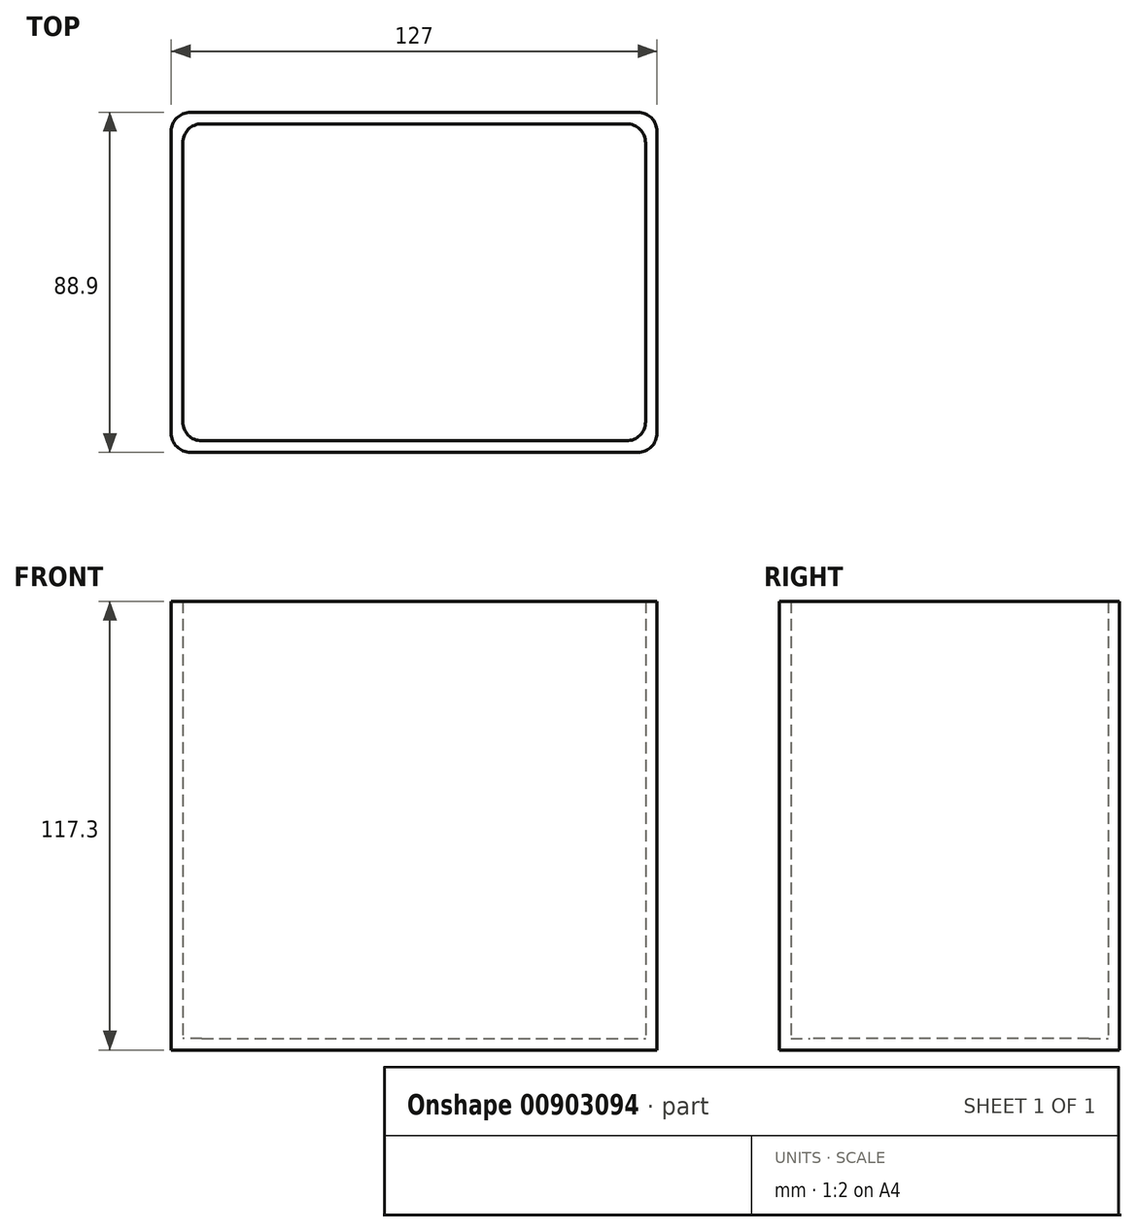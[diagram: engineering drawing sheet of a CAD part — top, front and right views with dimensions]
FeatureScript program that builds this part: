
annotation { "Feature Type Name" : "Feature", "Feature Type Description" : "" }
export const myFeature = defineFeature(function(context is Context, id is Id, definition is map)
    precondition{}
    {
        {
            var Q0;
            Q0=qCreatedBy(makeId("Top.planeOp"),FACE);
            var sketch = newSketch(context, id + "F0", { "sketchPlane" : qUnion([Q0])});
            skLineSegment(sketch, "E0.bottom", {"start": v(63.5, -44.45) * mm, "end": v(-63.5, -44.45) * mm});
            skLineSegment(sketch, "E0.top", {"start": v(63.5, 44.45) * mm, "end": v(-63.5, 44.45) * mm});
            skLineSegment(sketch, "E0.left", {"start": v(63.5, -44.45) * mm, "end": v(63.5, 44.45) * mm});
            skLineSegment(sketch, "E0.right", {"start": v(-63.5, -44.45) * mm, "end": v(-63.5, 44.45) * mm});
            skPoint(sketch, "E0.middle", {"position": v(0, 0) * mm});
            skSolve(sketch);
        }
        {
            var Q0;
            Q0 = qSketchRegion(id + "F0", true);
            extrude(context, id + "F1", {"entities" : qUnion([Q0]), "depth" : 3 * mm, "offsetDistance" : 25 * mm});
        }
        {
            var Q0;
            Q0=makeQuery(id+"F1.opExtrude","CAP_FACE",FACE,{"disambiguationData":[OSD([sQuery(id+"F0.wireOp",EDGE,"E0.bottom"),sQuery(id+"F0.wireOp",EDGE,"E0.top"),sQuery(id+"F0.wireOp",EDGE,"E0.left"),sQuery(id+"F0.wireOp",EDGE,"E0.right")])],"isStart":false});
            var sketch = newSketch(context, id + "F2", { "sketchPlane" : qUnion([Q0])});
            skLineSegment(sketch, "E1.bottom", {"start": v(-63.5, 44.45) * mm, "end": v(63.5, 44.45) * mm});
            skLineSegment(sketch, "E1.top", {"start": v(-63.5, -44.45) * mm, "end": v(63.5, -44.45) * mm});
            skLineSegment(sketch, "E1.left", {"start": v(-63.5, 44.45) * mm, "end": v(-63.5, -44.45) * mm});
            skLineSegment(sketch, "E1.right", {"start": v(63.5, 44.45) * mm, "end": v(63.5, -44.45) * mm});
            skPoint(sketch, "E1.middle", {"position": v(0, 0) * mm});
            skLineSegment(sketch, "E2.bottom", {"start": v(-60.5, 41.45) * mm, "end": v(60.5, 41.45) * mm});
            skLineSegment(sketch, "E2.top", {"start": v(-60.5, -41.45) * mm, "end": v(60.5, -41.45) * mm});
            skLineSegment(sketch, "E2.left", {"start": v(-60.5, 41.45) * mm, "end": v(-60.5, -41.45) * mm});
            skLineSegment(sketch, "E2.right", {"start": v(60.5, 41.45) * mm, "end": v(60.5, -41.45) * mm});
            skSolve(sketch);
        }
        {
            var Q0;
            Q0=makeQuery(id+"F2.imprint","IMPRINT",FACE,{"disambiguationData":[TD([[makeQuery(id+"F2.imprint","IMPRINT",EDGE,{"derivedFrom":sQuery(id+"F2.wireOp",EDGE,"E1.bottom")}),1.0]])]});
            extrude(context, id + "F3", {"entities" : qUnion([Q0]), "operationType" : NewBodyOperationType.ADD, "depth" : 114.3 * mm, "offsetDistance" : 25 * mm});
        }
        {
            var Q0;
            Q0=makeQuery(id+"F3.opExtrude","CAP_EDGE",EDGE,{"disambiguationData":[OSD([sQuery(id+"F2.wireOp",EDGE,"E2.top")])],"isStart":true});
            var Q1;
            Q1=makeQuery(id+"F3.opExtrude","CAP_EDGE",EDGE,{"disambiguationData":[OSD([sQuery(id+"F2.wireOp",EDGE,"E2.left")])],"isStart":true});
            var Q2;
            Q2=makeQuery(id+"F3.opExtrude","SWEPT_EDGE",EDGE,{"disambiguationData":[OSD([sQuery(id+"F2.wireOp",EDGE,"E2.top"),sQuery(id+"F2.wireOp",EDGE,"E2.left")])]});
            var Q3;
            Q3=makeQuery(id+"F3.opExtrude","SWEPT_EDGE",EDGE,{"disambiguationData":[OSD([sQuery(id+"F2.wireOp",EDGE,"E2.bottom"),sQuery(id+"F2.wireOp",EDGE,"E2.left")])]});
            var Q4;
            Q4=makeQuery(id+"F3.opExtrude","CAP_EDGE",EDGE,{"disambiguationData":[OSD([sQuery(id+"F2.wireOp",EDGE,"E2.bottom")])],"isStart":true});
            var Q5;
            Q5=makeQuery(id+"F3.opExtrude","SWEPT_EDGE",EDGE,{"disambiguationData":[OSD([sQuery(id+"F2.wireOp",EDGE,"E2.bottom"),sQuery(id+"F2.wireOp",EDGE,"E2.right")])]});
            var Q6;
            Q6=makeQuery(id+"F3.opExtrude","CAP_EDGE",EDGE,{"disambiguationData":[OSD([sQuery(id+"F2.wireOp",EDGE,"E2.right")])],"isStart":true});
            var Q7;
            Q7=makeQuery(id+"F3.opExtrude","SWEPT_EDGE",EDGE,{"disambiguationData":[OSD([sQuery(id+"F2.wireOp",EDGE,"E2.top"),sQuery(id+"F2.wireOp",EDGE,"E2.right")])]});
            var Q8;
            Q8=makeQuery(id+"F3.boolean.opBoolean","MERGE",EDGE,{"derivedFrom":[makeQuery(id+"F1.opExtrude","SWEPT_EDGE",EDGE,{"disambiguationData":[OSD([sQuery(id+"F0.wireOp",EDGE,"E0.bottom"),sQuery(id+"F0.wireOp",EDGE,"E0.left")])]}),makeQuery(id+"F3.opExtrude","SWEPT_EDGE",EDGE,{"disambiguationData":[OSD([sQuery(id+"F2.wireOp",EDGE,"E1.top"),sQuery(id+"F2.wireOp",EDGE,"E1.right")])]})]});
            var Q9;
            Q9=makeQuery(id+"F3.boolean.opBoolean","MERGE",EDGE,{"derivedFrom":[makeQuery(id+"F1.opExtrude","SWEPT_EDGE",EDGE,{"disambiguationData":[OSD([sQuery(id+"F0.wireOp",EDGE,"E0.top"),sQuery(id+"F0.wireOp",EDGE,"E0.left")])]}),makeQuery(id+"F3.opExtrude","SWEPT_EDGE",EDGE,{"disambiguationData":[OSD([sQuery(id+"F2.wireOp",EDGE,"E1.bottom"),sQuery(id+"F2.wireOp",EDGE,"E1.right")])]})]});
            var Q10;
            Q10=makeQuery(id+"F3.boolean.opBoolean","MERGE",EDGE,{"derivedFrom":[makeQuery(id+"F1.opExtrude","SWEPT_EDGE",EDGE,{"disambiguationData":[OSD([sQuery(id+"F0.wireOp",EDGE,"E0.top"),sQuery(id+"F0.wireOp",EDGE,"E0.right")])]}),makeQuery(id+"F3.opExtrude","SWEPT_EDGE",EDGE,{"disambiguationData":[OSD([sQuery(id+"F2.wireOp",EDGE,"E1.bottom"),sQuery(id+"F2.wireOp",EDGE,"E1.left")])]})]});
            var Q11;
            Q11=makeQuery(id+"F3.boolean.opBoolean","MERGE",EDGE,{"derivedFrom":[makeQuery(id+"F1.opExtrude","SWEPT_EDGE",EDGE,{"disambiguationData":[OSD([sQuery(id+"F0.wireOp",EDGE,"E0.bottom"),sQuery(id+"F0.wireOp",EDGE,"E0.right")])]}),makeQuery(id+"F3.opExtrude","SWEPT_EDGE",EDGE,{"disambiguationData":[OSD([sQuery(id+"F2.wireOp",EDGE,"E1.top"),sQuery(id+"F2.wireOp",EDGE,"E1.left")])]})]});
            fillet(context, id + "F4", {"entities" : qUnion([Q0, Q1, Q2, Q3, Q4, Q5, Q6, Q7, Q8, Q9, Q10, Q11]), "radius" : 5 * mm, "tangentPropagation" : true, "allowEdgeOverflow" : false});
        }
    });
